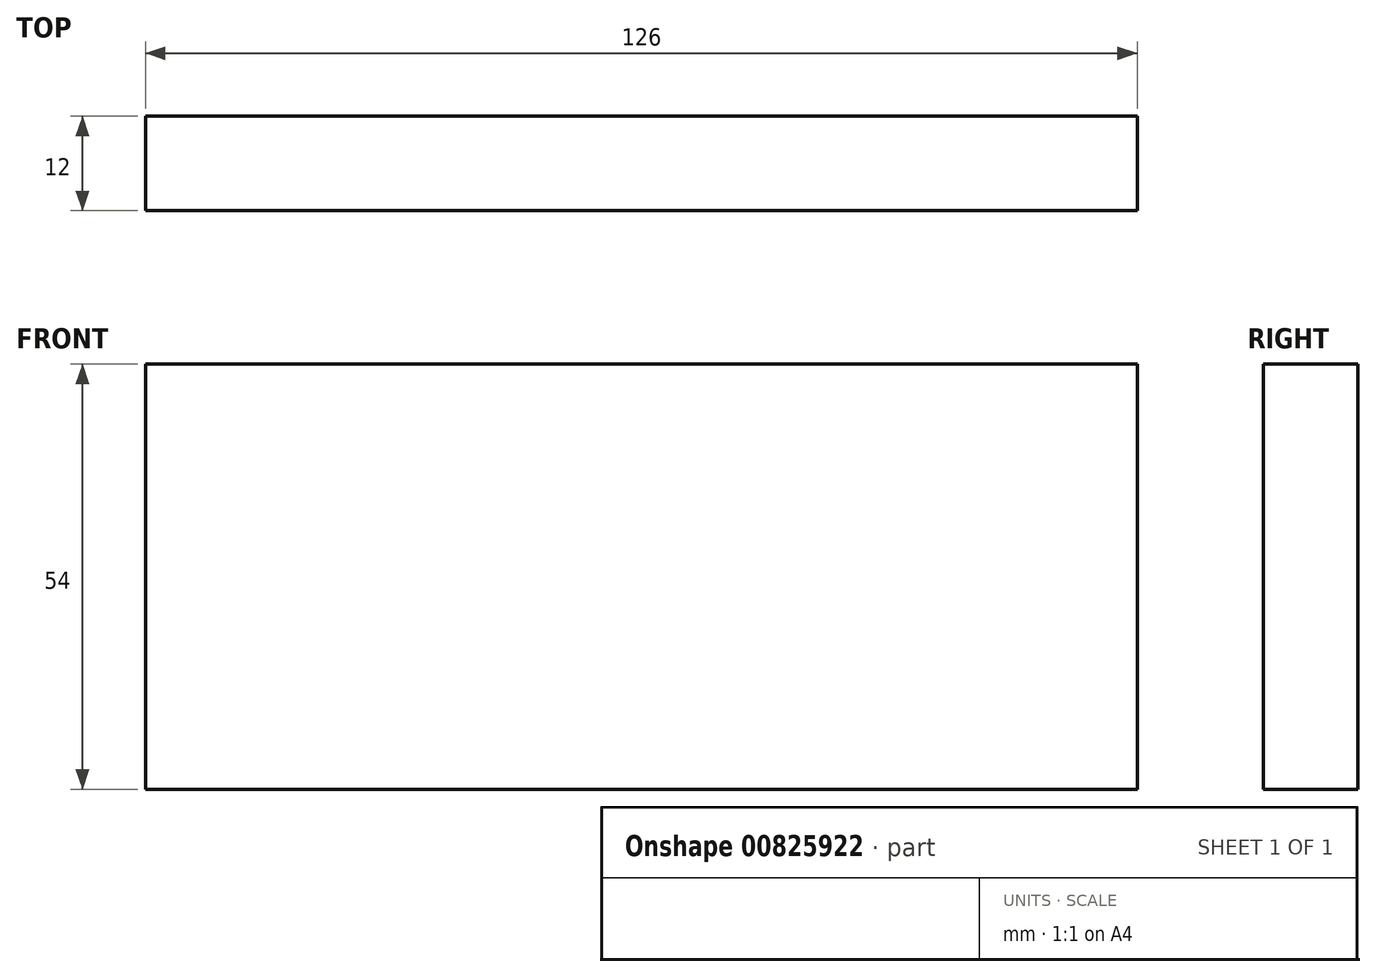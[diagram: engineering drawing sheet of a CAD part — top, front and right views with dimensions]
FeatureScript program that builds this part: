
annotation { "Feature Type Name" : "Feature", "Feature Type Description" : "" }
export const myFeature = defineFeature(function(context is Context, id is Id, definition is map)
    precondition{}
    {
        {
            var Q0;
            Q0=qCreatedBy(makeId("Right.planeOp"),FACE);
            var sketch = newSketch(context, id + "F0", { "sketchPlane" : qUnion([Q0])});
            skLineSegment(sketch, "E0.bottom", {"start": v(0, 0) * mm, "end": v(12, 0) * mm});
            skLineSegment(sketch, "E0.top", {"start": v(0, 54) * mm, "end": v(12, 54) * mm});
            skLineSegment(sketch, "E0.left", {"start": v(0, 0) * mm, "end": v(0, 54) * mm});
            skLineSegment(sketch, "E0.right", {"start": v(12, 0) * mm, "end": v(12, 54) * mm});
            skSolve(sketch);
        }
        {
            var Q0;
            Q0 = qSketchRegion(id + "F0", true);
            extrude(context, id + "F1", {"entities" : qUnion([Q0]), "depth" : 150 * mm, "offsetDistance" : 25 * mm});
        }
        {
            var Q0;
            Q0=makeQuery(id+"F1.opExtrude","SWEPT_FACE",FACE,{"disambiguationData":[OSD([sQuery(id+"F0.wireOp",EDGE,"E0.left")])]});
            var sketch = newSketch(context, id + "F2", { "sketchPlane" : qUnion([Q0])});
            skLineSegment(sketch, "E1", {"start": v(126, 54) * mm, "end": v(126, 0) * mm});
            skSolve(sketch);
        }
        {
            var Q0;
            Q0 = qSketchRegion(id + "F2", true);
            var Q1;
            {var subQ0=sQuery(id+"F2.wireOp",EDGE,"E1");Q1=makeQuery(id+"F2.imprint","IMPRINT",FACE,{"disambiguationData":[TD([[makeQuery(id+"F2.imprint","IMPRINT",EDGE,{"derivedFrom":subQ0}),1.0]])]});}
            extrude(context, id + "F3", {"entities" : qUnion([Q0, Q1]), "operationType" : NewBodyOperationType.REMOVE, "oppositeDirection" : true, "depth" : 25 * mm, "offsetDistance" : 25 * mm});
        }
    });
